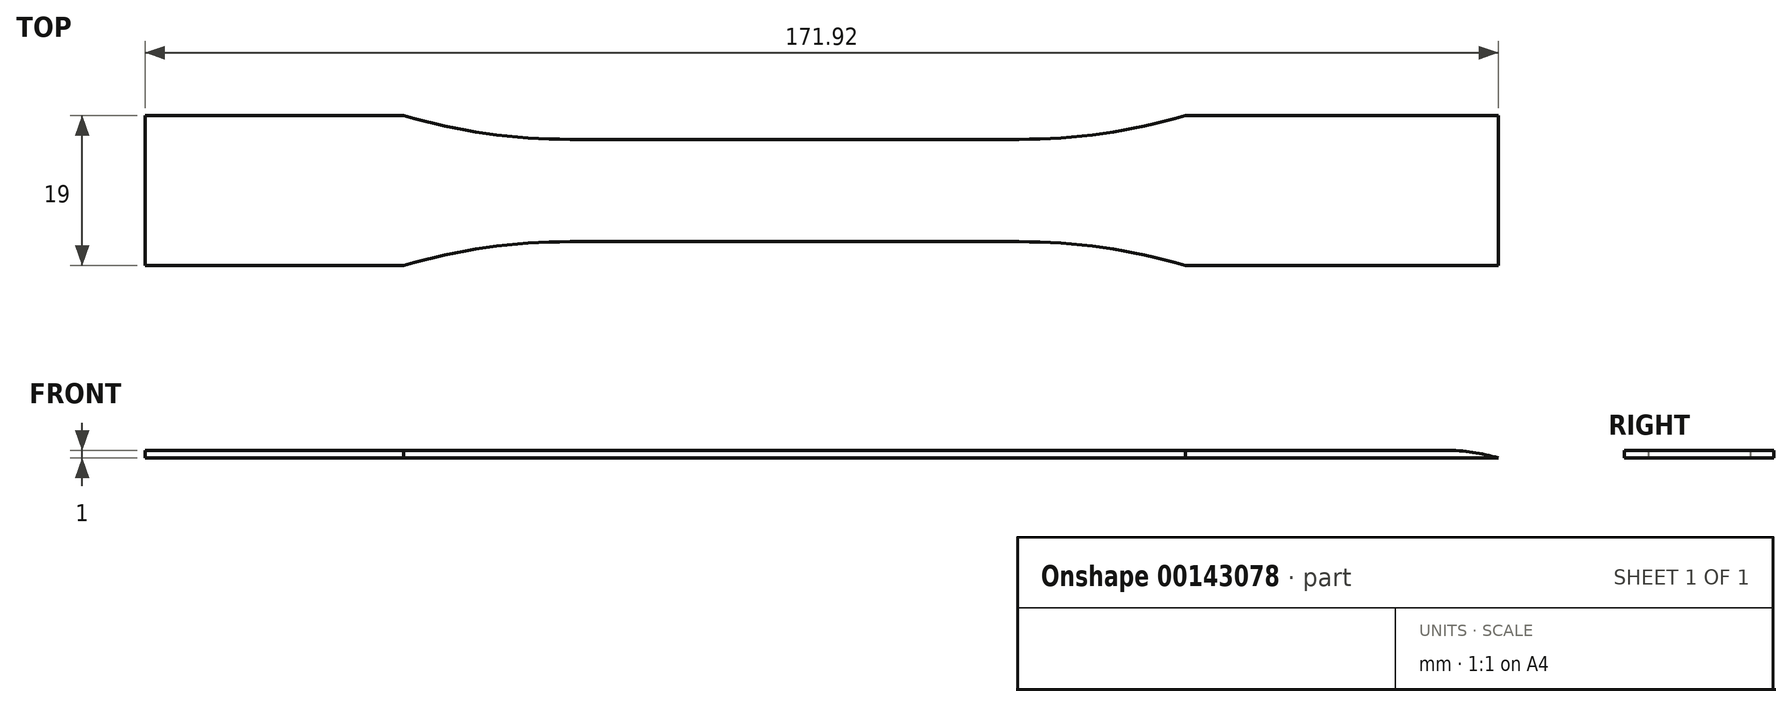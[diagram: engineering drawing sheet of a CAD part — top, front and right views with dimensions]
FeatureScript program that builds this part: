
annotation { "Feature Type Name" : "Feature", "Feature Type Description" : "" }
export const myFeature = defineFeature(function(context is Context, id is Id, definition is map)
    precondition{}
    {
        {
            var Q0;
            Q0=qCreatedBy(makeId("Top.planeOp"),FACE);
            var sketch = newSketch(context, id + "F0", { "sketchPlane" : qUnion([Q0])});
            skLineSegment(sketch, "E0.bottom", {"start": v(-82.5, 9.5) * mm, "end": v(-49.64, 9.5) * mm});
            skLineSegment(sketch, "E0.top", {"start": v(-82.5, -9.5) * mm, "end": v(-49.64, -9.5) * mm});
            skLineSegment(sketch, "E0.left", {"start": v(-82.5, 9.5) * mm, "end": v(-82.5, -9.5) * mm});
            skLineSegment(sketch, "E0.right", {"start": v(-49.64, 9.5) * mm, "end": v(-49.64, -9.5) * mm});
            skLineSegment(sketch, "E1.bottom", {"start": v(49.64, 9.5) * mm, "end": v(82.5, 9.5) * mm});
            skLineSegment(sketch, "E1.top", {"start": v(49.64, -9.5) * mm, "end": v(82.5, -9.5) * mm});
            skLineSegment(sketch, "E1.left", {"start": v(49.64, 9.5) * mm, "end": v(49.64, -9.5) * mm});
            skLineSegment(sketch, "E1.right", {"start": v(82.5, 9.5) * mm, "end": v(82.5, -9.5) * mm});
            skLineSegment(sketch, "E2.bottom", {"start": v(-28.5, 6.5) * mm, "end": v(28.5, 6.5) * mm});
            skLineSegment(sketch, "E2.top", {"start": v(-28.5, -6.5) * mm, "end": v(28.5, -6.5) * mm});
            skLineSegment(sketch, "E2.left", {"start": v(-28.5, 6.5) * mm, "end": v(-28.5, -6.5) * mm});
            skLineSegment(sketch, "E2.right", {"start": v(28.5, 6.5) * mm, "end": v(28.5, -6.5) * mm});
            skArc(sketch, "E3", {"start": v(-49.64, 9.5) * mm, "mid": v(-39.18, 7.25) * mm, "end": v(-28.5, 6.5) * mm});
            skLineSegment(sketch, "E4", {"start": v(0, 0) * mm, "end": v(0, -30.5) * mm, "construction": true});
            skLineSegment(sketch, "E5", {"start": v(0, 0) * mm, "end": v(92.54, 0) * mm, "construction": true});
            skArc(sketch, "E6.MirrorC", {"start": v(49.64, 9.5) * mm, "mid": v(39.18, 7.25) * mm, "end": v(28.5, 6.5) * mm});
            skArc(sketch, "E7.MirrorC", {"start": v(49.64, -9.5) * mm, "mid": v(39.18, -7.25) * mm, "end": v(28.5, -6.5) * mm});
            skArc(sketch, "E8.MirrorC", {"start": v(-49.64, -9.5) * mm, "mid": v(-39.18, -7.25) * mm, "end": v(-28.5, -6.5) * mm});
            skLineSegment(sketch, "E9", {"start": v(-49.64, -9.5) * mm, "end": v(0, -9.5) * mm, "construction": true});
            skPoint(sketch, "E9.endSnap0", {"position": v(0, -6.5) * mm});
            skLineSegment(sketch, "E10", {"start": v(0, -9.5) * mm, "end": v(49.64, -9.5) * mm, "construction": true});
            skSolve(sketch);
        }
        {
            var Q0;
            Q0 = qSketchRegion(id + "F0", true);
            extrude(context, id + "F1", {"entities" : qUnion([Q0]), "depth" : 1 * mm});
        }
        {
            var Q0;
            Q0=makeQuery(id+"F1.opExtrude","SWEPT_FACE",FACE,{"disambiguationData":[OSD([sQuery(id+"F0.wireOp",EDGE,"E1.top")])]});
            var sketch = newSketch(context, id + "F2", { "sketchPlane" : qUnion([Q0])});
            skLineSegment(sketch, "E11", {"start": v(82.5, 0) * mm, "end": v(89.42, 0) * mm});
            skLineSegment(sketch, "E12", {"start": v(82.5, 1) * mm, "end": v(82.5, 0) * mm});
            skLineSegment(sketch, "E13", {"start": v(82.5, 1) * mm, "end": v(89.42, 1) * mm});
            skLineSegment(sketch, "E14", {"start": v(89.42, 1) * mm, "end": v(89.42, 0) * mm});
            skSolve(sketch);
        }
        {
            var Q0;
            Q0 = qSketchRegion(id + "F2", true);
            extrude(context, id + "F3", {"entities" : qUnion([Q0]), "operationType" : NewBodyOperationType.ADD, "oppositeDirection" : true, "depth" : 19 * mm});
        }
        {
            var Q0;
            Q0=makeQuery(id+"F3.opExtrude","SWEPT_EDGE",EDGE,{"disambiguationData":[OSD([sQuery(id+"F2.wireOp",EDGE,"E13"),sQuery(id+"F2.wireOp",EDGE,"E14")])]});
            fillet(context, id + "F4", {"entities" : qUnion([Q0]), "radius" : 22.71 * mm, "tangentPropagation" : true, "allowEdgeOverflow" : false});
        }
    });
